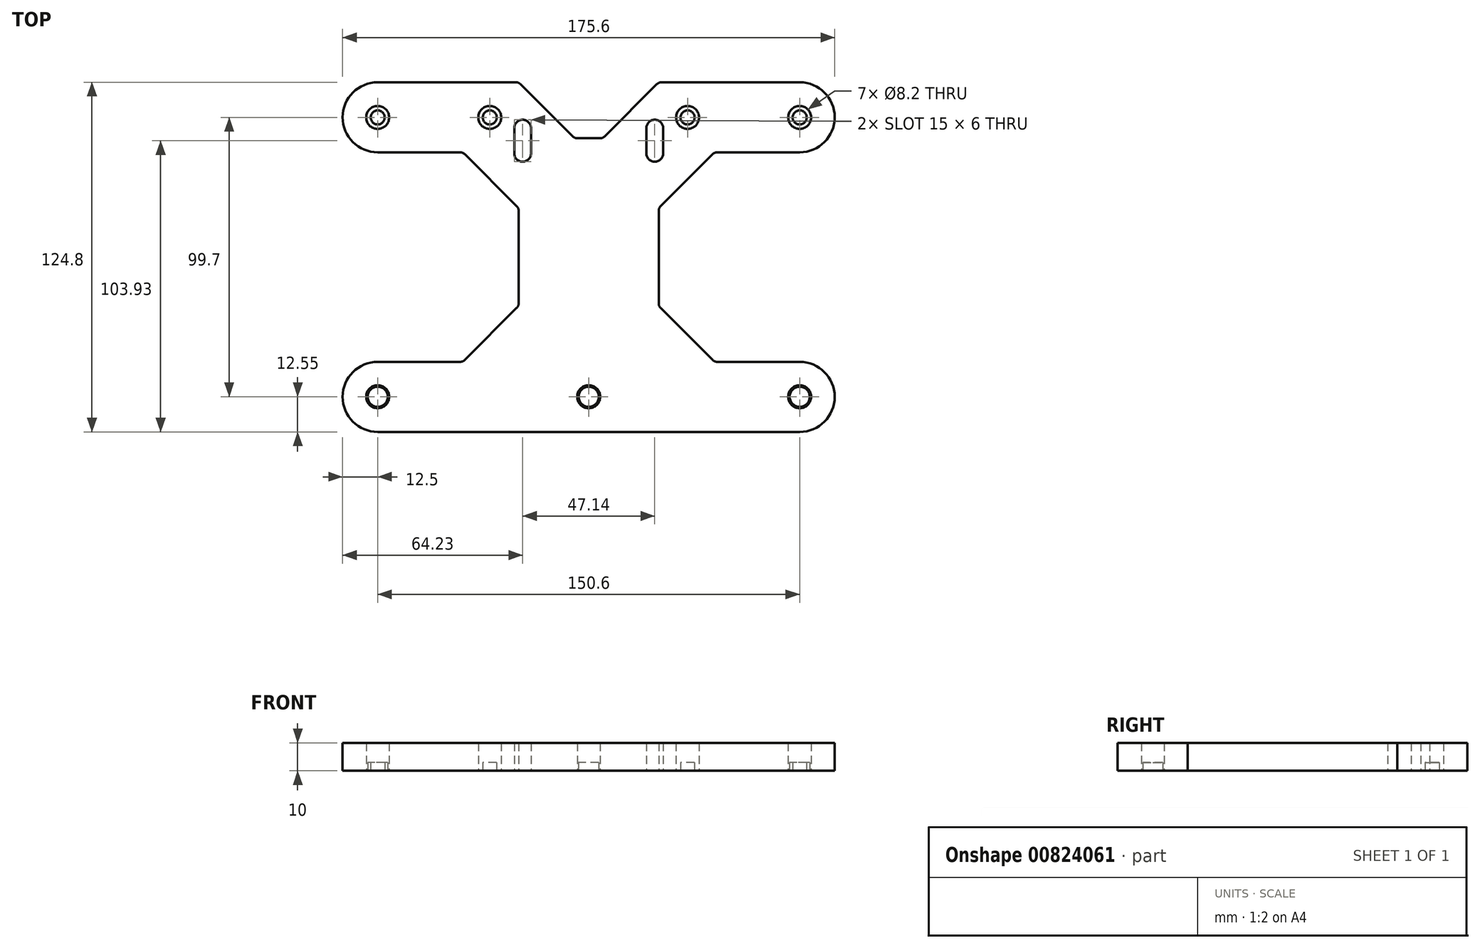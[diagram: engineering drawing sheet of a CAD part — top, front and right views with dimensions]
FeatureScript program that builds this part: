
annotation { "Feature Type Name" : "Feature", "Feature Type Description" : "" }
export const myFeature = defineFeature(function(context is Context, id is Id, definition is map)
    precondition{}
    {
        {
            var Q0;
            Q0=qCreatedBy(makeId("Top.planeOp"),FACE);
            var sketch = newSketch(context, id + "F0", { "sketchPlane" : qUnion([Q0])});
            skLineSegment(sketch, "E0", {"start": v(-75.3, -62.4) * mm, "end": v(75.3, -62.4) * mm});
            skLineSegment(sketch, "E1", {"start": v(75.3, -37.4) * mm, "end": v(45.87, -37.4) * mm});
            skLineSegment(sketch, "E2", {"start": v(-75.3, -37.4) * mm, "end": v(-45.87, -37.4) * mm});
            skLineSegment(sketch, "E3", {"start": v(-26.57, 46.03) * mm, "end": v(-26.57, 37.03) * mm});
            skLineSegment(sketch, "E4", {"start": v(-25, -16.53) * mm, "end": v(-25, 16.53) * mm});
            skLineSegment(sketch, "E5", {"start": v(-20.57, 37.03) * mm, "end": v(-20.57, 46.03) * mm});
            skLineSegment(sketch, "E6", {"start": v(5.69, 43.09) * mm, "end": v(24.31, 61.71) * mm});
            skLineSegment(sketch, "E7", {"start": v(-44.21, -36.71) * mm, "end": v(-25.69, -18.19) * mm});
            skLineSegment(sketch, "E8", {"start": v(-25.69, 18.19) * mm, "end": v(-44.21, 36.71) * mm});
            skLineSegment(sketch, "E9", {"start": v(44.21, 36.71) * mm, "end": v(25.69, 18.19) * mm});
            skLineSegment(sketch, "E10", {"start": v(25.69, -18.19) * mm, "end": v(44.21, -36.71) * mm});
            skLineSegment(sketch, "E11", {"start": v(20.57, 46.03) * mm, "end": v(20.57, 37.03) * mm});
            skLineSegment(sketch, "E12", {"start": v(25, 16.53) * mm, "end": v(25, -16.53) * mm});
            skLineSegment(sketch, "E13", {"start": v(26.57, 37.03) * mm, "end": v(26.57, 46.03) * mm});
            skLineSegment(sketch, "E14", {"start": v(-24.31, 61.71) * mm, "end": v(-5.69, 43.09) * mm});
            skLineSegment(sketch, "E15", {"start": v(75.3, 37.4) * mm, "end": v(45.87, 37.4) * mm});
            skLineSegment(sketch, "E16", {"start": v(-75.3, 37.4) * mm, "end": v(-45.87, 37.4) * mm});
            skLineSegment(sketch, "E17", {"start": v(-4.03, 42.4) * mm, "end": v(4.03, 42.4) * mm});
            skLineSegment(sketch, "E18", {"start": v(75.3, 62.4) * mm, "end": v(25.97, 62.4) * mm});
            skLineSegment(sketch, "E19", {"start": v(-25.97, 62.4) * mm, "end": v(-75.3, 62.4) * mm});
            skArc(sketch, "E20", {"start": v(-75.3, 62.4) * mm, "mid": v(-87.8, 49.9) * mm, "end": v(-75.3, 37.4) * mm});
            skArc(sketch, "E21", {"start": v(-75.3, -37.4) * mm, "mid": v(-87.8, -49.9) * mm, "end": v(-75.3, -62.4) * mm});
            skArc(sketch, "E22", {"start": v(75.3, -62.4) * mm, "mid": v(87.8, -49.9) * mm, "end": v(75.3, -37.4) * mm});
            skArc(sketch, "E23", {"start": v(75.3, 37.4) * mm, "mid": v(87.8, 49.9) * mm, "end": v(75.3, 62.4) * mm});
            skCircle(sketch, "E24", {"center": v(0, -49.85) * mm, "radius": 3.6 * mm});
            skCircle(sketch, "E25", {"center": v(75.3, -49.85) * mm, "radius": 3.6 * mm});
            skCircle(sketch, "E26", {"center": v(-75.3, -49.85) * mm, "radius": 3.6 * mm});
            skArc(sketch, "E27", {"start": v(26.57, 46.03) * mm, "mid": v(23.57, 49.03) * mm, "end": v(20.57, 46.03) * mm});
            skArc(sketch, "E28", {"start": v(20.57, 37.03) * mm, "mid": v(23.57, 34.03) * mm, "end": v(26.57, 37.03) * mm});
            skArc(sketch, "E29", {"start": v(-20.57, 46.03) * mm, "mid": v(-23.57, 49.03) * mm, "end": v(-26.57, 46.03) * mm});
            skArc(sketch, "E30", {"start": v(-26.57, 37.03) * mm, "mid": v(-23.57, 34.03) * mm, "end": v(-20.57, 37.03) * mm});
            skCircle(sketch, "E31", {"center": v(-35.3, 49.85) * mm, "radius": 2.5 * mm});
            skCircle(sketch, "E32", {"center": v(35.3, 49.85) * mm, "radius": 2.5 * mm});
            skCircle(sketch, "E33", {"center": v(75.3, 49.85) * mm, "radius": 2.5 * mm});
            skCircle(sketch, "E34", {"center": v(-75.3, 49.85) * mm, "radius": 2.5 * mm});
            skArc(sketch, "E35", {"start": v(-5.69, 43.09) * mm, "mid": v(-4.93, 42.58) * mm, "end": v(-4.03, 42.4) * mm});
            skArc(sketch, "E36", {"start": v(4.03, 42.4) * mm, "mid": v(4.93, 42.58) * mm, "end": v(5.69, 43.09) * mm});
            skArc(sketch, "E37", {"start": v(45.87, 37.4) * mm, "mid": v(44.97, 37.22) * mm, "end": v(44.21, 36.71) * mm});
            skArc(sketch, "E38", {"start": v(25.69, 18.19) * mm, "mid": v(25.18, 17.43) * mm, "end": v(25, 16.53) * mm});
            skArc(sketch, "E39", {"start": v(44.21, -36.71) * mm, "mid": v(44.97, -37.22) * mm, "end": v(45.87, -37.4) * mm});
            skArc(sketch, "E40", {"start": v(25, -16.53) * mm, "mid": v(25.18, -17.43) * mm, "end": v(25.69, -18.19) * mm});
            skArc(sketch, "E41", {"start": v(-45.87, -37.4) * mm, "mid": v(-44.97, -37.22) * mm, "end": v(-44.21, -36.71) * mm});
            skArc(sketch, "E42", {"start": v(-25.69, -18.19) * mm, "mid": v(-25.18, -17.43) * mm, "end": v(-25, -16.53) * mm});
            skArc(sketch, "E43", {"start": v(-25, 16.53) * mm, "mid": v(-25.18, 17.43) * mm, "end": v(-25.69, 18.19) * mm});
            skArc(sketch, "E44", {"start": v(-44.21, 36.71) * mm, "mid": v(-44.97, 37.22) * mm, "end": v(-45.87, 37.4) * mm});
            skArc(sketch, "E45", {"start": v(-24.31, 61.71) * mm, "mid": v(-25.07, 62.22) * mm, "end": v(-25.97, 62.4) * mm});
            skArc(sketch, "E46", {"start": v(25.97, 62.4) * mm, "mid": v(25.07, 62.22) * mm, "end": v(24.31, 61.71) * mm});
            skCircle(sketch, "E47.0", {"center": v(-75.3, -49.85) * mm, "radius": 4.1 * mm});
            skCircle(sketch, "E48.0", {"center": v(0, -49.85) * mm, "radius": 4.1 * mm});
            skCircle(sketch, "E49.0", {"center": v(75.3, -49.85) * mm, "radius": 4.1 * mm});
            skCircle(sketch, "E50.0", {"center": v(75.3, 49.85) * mm, "radius": 4.1 * mm});
            skCircle(sketch, "E51.0", {"center": v(35.3, 49.85) * mm, "radius": 4.1 * mm});
            skCircle(sketch, "E52.0", {"center": v(-35.3, 49.85) * mm, "radius": 4.1 * mm});
            skCircle(sketch, "E53.0", {"center": v(-75.3, 49.85) * mm, "radius": 4.1 * mm});
            skSolve(sketch);
        }
        {
            var Q0;
            Q0 = qSketchRegion(id + "F0", true);
            extrude(context, id + "F1", {"entities" : qUnion([Q0]), "depth" : 10 * mm, "offsetDistance" : 25 * mm});
        }
        {
            var Q0;
            Q0=makeQuery(id+"F0.imprint","IMPRINT",FACE,{"disambiguationData":[TD([[makeQuery(id+"F0.imprint","IMPRINT",EDGE,{"derivedFrom":sQuery(id+"F0.wireOp",EDGE,"E26")}),1.0]])]});
            var Q1;
            Q1=makeQuery(id+"F0.imprint","IMPRINT",FACE,{"disambiguationData":[TD([[makeQuery(id+"F0.imprint","IMPRINT",EDGE,{"derivedFrom":sQuery(id+"F0.wireOp",EDGE,"E24")}),1.0]])]});
            var Q2;
            Q2=makeQuery(id+"F0.imprint","IMPRINT",FACE,{"disambiguationData":[TD([[makeQuery(id+"F0.imprint","IMPRINT",EDGE,{"derivedFrom":sQuery(id+"F0.wireOp",EDGE,"E25")}),1.0]])]});
            var Q3;
            Q3=makeQuery(id+"F0.imprint","IMPRINT",FACE,{"disambiguationData":[TD([[makeQuery(id+"F0.imprint","IMPRINT",EDGE,{"derivedFrom":sQuery(id+"F0.wireOp",EDGE,"E33")}),1.0]])]});
            var Q4;
            Q4=makeQuery(id+"F0.imprint","IMPRINT",FACE,{"disambiguationData":[TD([[makeQuery(id+"F0.imprint","IMPRINT",EDGE,{"derivedFrom":sQuery(id+"F0.wireOp",EDGE,"E32")}),1.0]])]});
            var Q5;
            Q5=makeQuery(id+"F0.imprint","IMPRINT",FACE,{"disambiguationData":[TD([[makeQuery(id+"F0.imprint","IMPRINT",EDGE,{"derivedFrom":sQuery(id+"F0.wireOp",EDGE,"E31")}),1.0]])]});
            var Q6;
            Q6=makeQuery(id+"F0.imprint","IMPRINT",FACE,{"disambiguationData":[TD([[makeQuery(id+"F0.imprint","IMPRINT",EDGE,{"derivedFrom":sQuery(id+"F0.wireOp",EDGE,"E34")}),1.0]])]});
            extrude(context, id + "F2", {"entities" : qUnion([Q0, Q1, Q2, Q3, Q4, Q5, Q6]), "operationType" : NewBodyOperationType.ADD, "depth" : 3 * mm, "offsetDistance" : 25 * mm});
        }
    });
